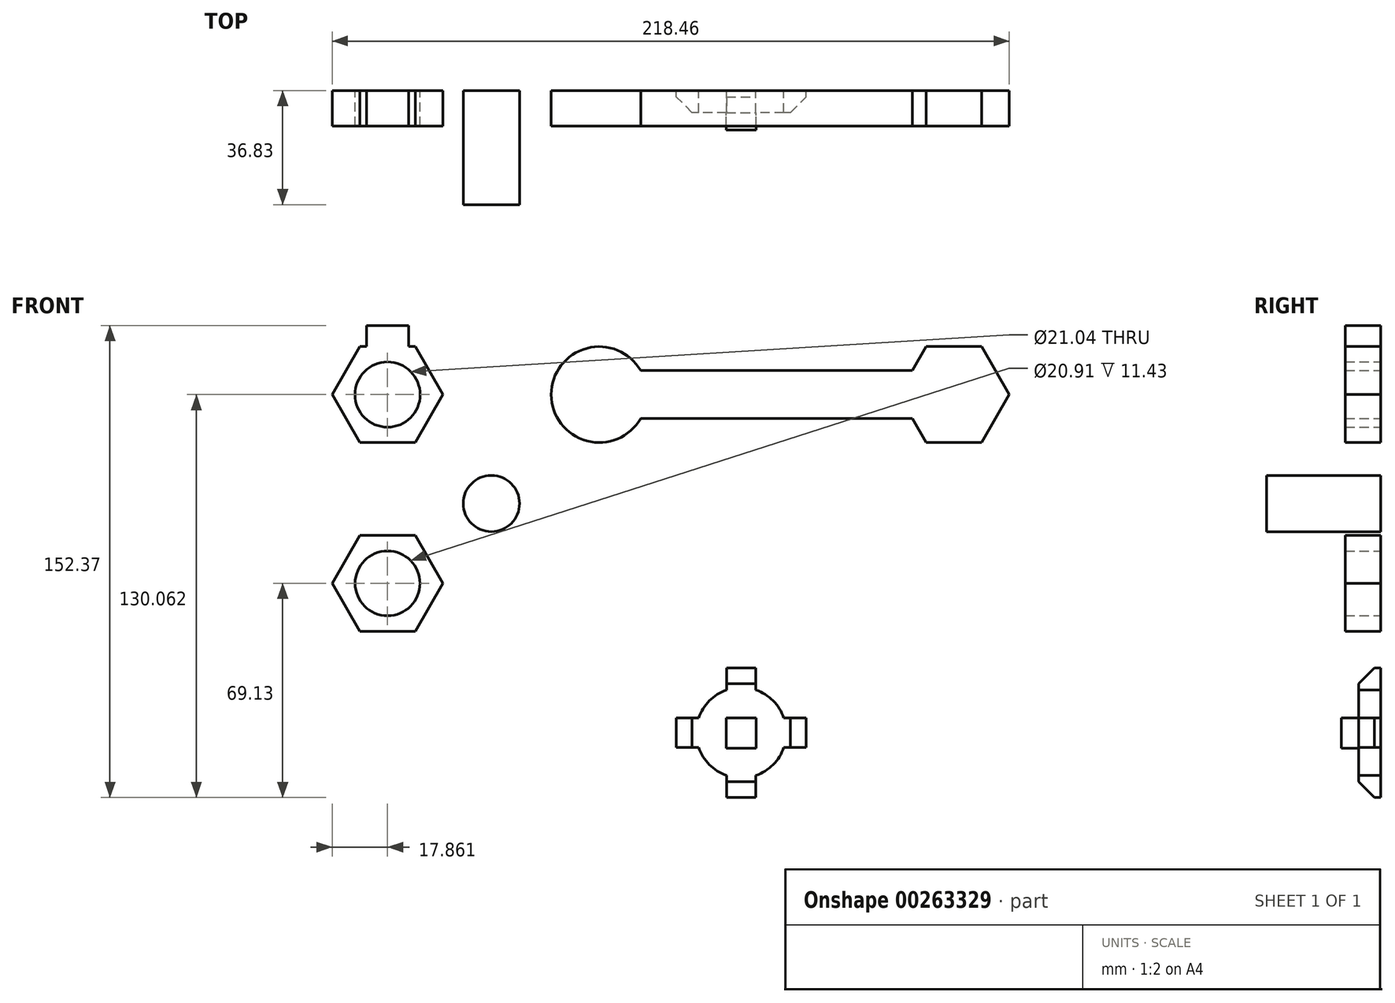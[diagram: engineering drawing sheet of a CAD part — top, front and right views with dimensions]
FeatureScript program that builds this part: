
annotation { "Feature Type Name" : "Feature", "Feature Type Description" : "" }
export const myFeature = defineFeature(function(context is Context, id is Id, definition is map)
    precondition{}
    {
        {
            var Q0;
            Q0=qCreatedBy(makeId("Front.planeOp"),FACE);
            var sketch = newSketch(context, id + "F0", { "sketchPlane" : qUnion([Q0])});
            skCircle(sketch, "E0.cCircle", {"center": v(-68.29, 60.93) * mm, "radius": 15.47 * mm, "construction": true});
            skLineSegment(sketch, "E0.0", {"start": v(-77.22, 76.4) * mm, "end": v(-59.36, 76.4) * mm});
            skLineSegment(sketch, "E0.1", {"start": v(-59.36, 76.4) * mm, "end": v(-50.43, 60.93) * mm});
            skLineSegment(sketch, "E0.2", {"start": v(-50.43, 60.93) * mm, "end": v(-59.36, 45.46) * mm});
            skLineSegment(sketch, "E0.3", {"start": v(-59.36, 45.46) * mm, "end": v(-77.22, 45.46) * mm});
            skLineSegment(sketch, "E0.4", {"start": v(-77.22, 45.46) * mm, "end": v(-86.15, 60.93) * mm});
            skLineSegment(sketch, "E0.5", {"start": v(-86.15, 60.93) * mm, "end": v(-77.22, 76.4) * mm});
            skPoint(sketch, "E0.0.midPoint", {"position": v(-68.29, 76.4) * mm});
            skCircle(sketch, "E1", {"center": v(-68.29, 60.93) * mm, "radius": 10.52 * mm});
            skCircle(sketch, "E2.cCircle", {"center": v(0, 60.93) * mm, "radius": 15.47 * mm, "construction": true});
            skPoint(sketch, "E2.0.midPoint", {"position": v(0, 76.4) * mm});
            skPoint(sketch, "E3.oppositeSnap0", {"position": v(13.4, 53.2) * mm});
            skLineSegment(sketch, "E3.bottom", {"start": v(13.4, 68.67) * mm, "end": v(114.45, 68.67) * mm});
            skLineSegment(sketch, "E3.top", {"start": v(13.4, 53.2) * mm, "end": v(114.45, 53.2) * mm});
            skLineSegment(sketch, "E3.left", {"start": v(13.4, 68.67) * mm, "end": v(13.4, 53.2) * mm});
            skLineSegment(sketch, "E3.right", {"start": v(114.45, 68.67) * mm, "end": v(114.45, 53.2) * mm});
            skCircle(sketch, "E4.cCircle", {"center": v(114.45, 60.93) * mm, "radius": 15.47 * mm, "construction": true});
            skLineSegment(sketch, "E4.0", {"start": v(105.52, 76.4) * mm, "end": v(123.38, 76.4) * mm});
            skLineSegment(sketch, "E4.1", {"start": v(123.38, 76.4) * mm, "end": v(132.31, 60.93) * mm});
            skLineSegment(sketch, "E4.2", {"start": v(132.31, 60.93) * mm, "end": v(123.38, 45.46) * mm});
            skLineSegment(sketch, "E4.3", {"start": v(123.38, 45.46) * mm, "end": v(105.52, 45.46) * mm});
            skLineSegment(sketch, "E4.4", {"start": v(105.52, 45.46) * mm, "end": v(96.6, 60.93) * mm});
            skLineSegment(sketch, "E4.5", {"start": v(96.6, 60.93) * mm, "end": v(105.52, 76.4) * mm});
            skPoint(sketch, "E4.0.midPoint", {"position": v(114.45, 76.4) * mm});
            skCircle(sketch, "E5", {"center": v(0, 60.93) * mm, "radius": 15.47 * mm});
            skCircle(sketch, "E6.cCircle", {"center": v(-68.29, 0) * mm, "radius": 15.47 * mm, "construction": true});
            skPoint(sketch, "E6.cCircle.centerSnap0", {"position": v(-68.29, 45.46) * mm});
            skPoint(sketch, "E6.cCircle.perimeterSnap0", {"position": v(-54.9, 53.2) * mm});
            skLineSegment(sketch, "E6.0", {"start": v(-50.43, 0) * mm, "end": v(-59.36, -15.47) * mm});
            skLineSegment(sketch, "E6.1", {"start": v(-59.36, -15.47) * mm, "end": v(-77.22, -15.47) * mm});
            skLineSegment(sketch, "E6.2", {"start": v(-77.22, -15.47) * mm, "end": v(-86.15, 0) * mm});
            skLineSegment(sketch, "E6.3", {"start": v(-86.15, 0) * mm, "end": v(-77.22, 15.47) * mm});
            skLineSegment(sketch, "E6.4", {"start": v(-77.22, 15.47) * mm, "end": v(-59.36, 15.47) * mm});
            skLineSegment(sketch, "E6.5", {"start": v(-59.36, 15.47) * mm, "end": v(-50.43, 0) * mm});
            skPoint(sketch, "E6.0.midPoint", {"position": v(-54.9, -7.73) * mm});
            skPoint(sketch, "E6.0.midPoint.positionSnap0", {"position": v(-54.9, 53.2) * mm});
            skCircle(sketch, "E7", {"center": v(-68.29, 0) * mm, "radius": 10.46 * mm});
            skLineSegment(sketch, "E8.0", {"start": v(-75.12, 83.24) * mm, "end": v(-61.45, 83.24) * mm});
            skLineSegment(sketch, "E8.1", {"start": v(-61.45, 83.24) * mm, "end": v(-61.45, 69.56) * mm});
            skLineSegment(sketch, "E8.3", {"start": v(-75.12, 69.56) * mm, "end": v(-75.12, 83.24) * mm});
            skPoint(sketch, "E8.0.midPoint", {"position": v(-68.29, 83.24) * mm});
            skLineSegment(sketch, "E9", {"start": v(-75.12, 69.56) * mm, "end": v(-68.29, 76.4) * mm});
            skLineSegment(sketch, "E10", {"start": v(-61.45, 69.56) * mm, "end": v(-68.29, 76.4) * mm});
            skSolve(sketch);
        }
        {
            var Q0;
            Q0=qSketchRegion(id+"F0",true);
            extrude(context, id + "F1", {"entities" : qUnion([Q0]), "depth" : 11.43 * mm});
        }
        {
            var Q0;
            Q0=qCreatedBy(makeId("Front.planeOp"),FACE);
            var sketch = newSketch(context, id + "F3", { "sketchPlane" : qUnion([Q0])});
            skCircle(sketch, "E11", {"center": v(45.85, -48.2) * mm, "radius": 14.56 * mm});
            skLineSegment(sketch, "E12.bottom", {"start": v(45.85, -48.2) * mm, "end": v(45.85, -48.2) * mm});
            skLineSegment(sketch, "E12.top", {"start": v(45.85, -62.76) * mm, "end": v(45.85, -62.76) * mm});
            skLineSegment(sketch, "E13.top", {"start": v(45.85, -33.64) * mm, "end": v(45.85, -33.64) * mm});
            skLineSegment(sketch, "E14.right", {"start": v(60.42, -48.2) * mm, "end": v(60.42, -48.2) * mm});
            skLineSegment(sketch, "E15.right", {"start": v(31.3, -48.2) * mm, "end": v(31.3, -48.2) * mm});
            skPoint(sketch, "E16.0.midPoint", {"position": v(45.85, -69.13) * mm});
            skLineSegment(sketch, "E17.bottom", {"start": v(66.78, -52.96) * mm, "end": v(24.92, -52.96) * mm});
            skLineSegment(sketch, "E17.top", {"start": v(66.78, -43.43) * mm, "end": v(24.92, -43.43) * mm});
            skLineSegment(sketch, "E17.left", {"start": v(66.78, -52.96) * mm, "end": v(66.78, -43.43) * mm});
            skLineSegment(sketch, "E17.right", {"start": v(24.92, -52.96) * mm, "end": v(24.92, -43.43) * mm});
            skLineSegment(sketch, "E18.bottom", {"start": v(41.11, -69.13) * mm, "end": v(50.6, -69.13) * mm});
            skLineSegment(sketch, "E18.top", {"start": v(41.11, -27.27) * mm, "end": v(50.6, -27.27) * mm});
            skLineSegment(sketch, "E18.left", {"start": v(41.11, -69.13) * mm, "end": v(41.11, -27.27) * mm});
            skLineSegment(sketch, "E18.right", {"start": v(50.6, -69.13) * mm, "end": v(50.6, -27.27) * mm});
            skSolve(sketch);
        }
        {
            var Q0;
            Q0=qSketchRegion(id+"F3",true);
            extrude(context, id + "F4", {"entities" : qUnion([Q0]), "depth" : 7.11 * mm});
        }
        {
            var Q0;
            Q0=makeQuery(id+"F4.opExtrude","CAP_EDGE",EDGE,{"disambiguationData":[OSD([sQuery(id+"F3.wireOp",EDGE,"E18.top")])],"isStart":false});
            var Q1;
            Q1=makeQuery(id+"F4.opExtrude","CAP_EDGE",EDGE,{"disambiguationData":[OSD([sQuery(id+"F3.wireOp",EDGE,"E17.left")])],"isStart":false});
            var Q2;
            Q2=makeQuery(id+"F4.opExtrude","CAP_EDGE",EDGE,{"disambiguationData":[OSD([sQuery(id+"F3.wireOp",EDGE,"E18.bottom")])],"isStart":false});
            var Q3;
            Q3=makeQuery(id+"F4.opExtrude","CAP_EDGE",EDGE,{"disambiguationData":[OSD([sQuery(id+"F3.wireOp",EDGE,"E17.right")])],"isStart":false});
            var Q4;
            {var subQ0=sQuery(id+"F3.wireOp",EDGE,"E11");Q4=makeQuery(id+"F4.opExtrude","CAP_EDGE",EDGE,{"disambiguationData":[OSD([subQ0]),TDD([makeQuery(id+"F3.imprint","IMPRINT",EDGE,{"disambiguationData":[TD([[makeQuery(id+"F3.imprint","INTERSECT",VERTEX,{"disambiguationData":[OD(0.0)],"derivedFrom":[subQ0,sQuery(id+"F3.wireOp",EDGE,"E18.right")]}),1.0]])],"derivedFrom":subQ0})])],"isStart":false});}
            var Q5;
            {var subQ0=sQuery(id+"F3.wireOp",EDGE,"E11");Q5=makeQuery(id+"F4.opExtrude","CAP_EDGE",EDGE,{"disambiguationData":[OSD([subQ0]),TDD([makeQuery(id+"F3.imprint","IMPRINT",EDGE,{"disambiguationData":[TD([[makeQuery(id+"F3.imprint","INTERSECT",VERTEX,{"disambiguationData":[OD(1.0)],"derivedFrom":[subQ0,sQuery(id+"F3.wireOp",EDGE,"E18.right")]}),-1.0]])],"derivedFrom":subQ0})])],"isStart":false});}
            var Q6;
            {var subQ0=sQuery(id+"F3.wireOp",EDGE,"E11");Q6=makeQuery(id+"F4.opExtrude","CAP_EDGE",EDGE,{"disambiguationData":[OSD([subQ0]),TDD([makeQuery(id+"F3.imprint","IMPRINT",EDGE,{"disambiguationData":[TD([[makeQuery(id+"F3.imprint","INTERSECT",VERTEX,{"disambiguationData":[OD(0.0)],"derivedFrom":[subQ0,sQuery(id+"F3.wireOp",EDGE,"E18.left")]}),-1.0]])],"derivedFrom":subQ0})])],"isStart":false});}
            var Q7;
            {var subQ0=sQuery(id+"F3.wireOp",EDGE,"E11");Q7=makeQuery(id+"F4.opExtrude","CAP_EDGE",EDGE,{"disambiguationData":[OSD([subQ0]),TDD([makeQuery(id+"F3.imprint","IMPRINT",EDGE,{"disambiguationData":[TD([[makeQuery(id+"F3.imprint","INTERSECT",VERTEX,{"disambiguationData":[OD(0.0)],"derivedFrom":[subQ0,sQuery(id+"F3.wireOp",EDGE,"E17.bottom")]}),-1.0]])],"derivedFrom":subQ0})])],"isStart":false});}
            chamfer(context, id + "F5", {"entities" : qUnion([Q0, Q1, Q2, Q3, Q4, Q5, Q6, Q7]), "width" : 5.08 * mm, "tangentPropagation" : true});
        }
        {
            var Q0;
            Q0=qCreatedBy(makeId("Front.planeOp"),FACE);
            var sketch = newSketch(context, id + "F6", { "sketchPlane" : qUnion([Q0])});
            skLineSegment(sketch, "E19.bottom", {"start": v(50.66, -43.4) * mm, "end": v(40.95, -43.4) * mm});
            skLineSegment(sketch, "E19.top", {"start": v(50.66, -53.23) * mm, "end": v(40.95, -53.23) * mm});
            skLineSegment(sketch, "E19.left", {"start": v(50.66, -43.4) * mm, "end": v(50.66, -53.23) * mm});
            skLineSegment(sketch, "E19.right", {"start": v(40.95, -43.4) * mm, "end": v(40.95, -53.23) * mm});
            skSolve(sketch);
        }
        {
            var Q0;
            Q0=qSketchRegion(id+"F6",true);
            extrude(context, id + "F7", {"entities" : qUnion([Q0]), "operationType" : NewBodyOperationType.ADD, "depth" : 12.7 * mm});
        }
        {
            var Q0;
            Q0=qCreatedBy(makeId("Front.planeOp"),FACE);
            var sketch = newSketch(context, id + "F8", { "sketchPlane" : qUnion([Q0])});
            skCircle(sketch, "E20", {"center": v(-34.77, 25.77) * mm, "radius": 9.08 * mm});
            skSolve(sketch);
        }
        {
            var Q0;
            Q0=qSketchRegion(id+"F8",true);
            extrude(context, id + "F9", {"entities" : qUnion([Q0]), "operationType" : NewBodyOperationType.ADD, "depth" : 36.83 * mm});
        }
        {
            var Q0;
            Q0 = qSketchRegion(id + "F8", true);
            extrude(context, id + "F10", {"entities" : qUnion([Q0]), "depth" : 36.83 * mm});
        }
    });
